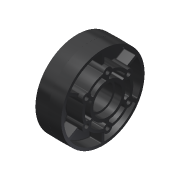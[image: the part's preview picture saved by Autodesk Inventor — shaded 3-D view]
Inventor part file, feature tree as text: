
AUTODESK INVENTOR PART (.ipt)
format: ipt  version: 2013 (Build 170138000, 138)  size: 1,176,576 bytes
history: native  units: in
note: dims shown in document units (in); Inventor stores cm internally (conversion verified against a paired STEP export)
features: fillet x2, imported_body x2, other x1
ambient origin geometry x8: Origin, YZ Plane, XZ Plane, XY Plane, X Axis, Y Axis, Z Axis, Center Point
feature tree (5):
  fillet  "Fillet10"  [1 undecoded]
  other  "4in 2013 Hub1"
  fillet  "Fillet9"  [1 undecoded]
  imported_body  "Base1"
  imported_body  "Base2"
note: 2 required parameter values undecoded (feature->parameter linkage not recoverable at this tier; creation-order binding heuristic only, values carry confidence <= 0.55)
